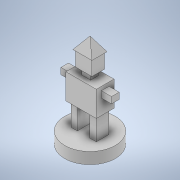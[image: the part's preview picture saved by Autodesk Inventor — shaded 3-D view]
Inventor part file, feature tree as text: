
AUTODESK INVENTOR PART (.ipt)
format: ipt  version: 2020 (Build 240168000, 168)  size: 219,648 bytes
history: native  units: in
note: dims shown in document units (in); Inventor stores cm internally (conversion verified against a paired STEP export)
features: extrude x10, sketch x10
ambient origin geometry x8: Origin, YZ Plane, XZ Plane, XY Plane, X Axis, Y Axis, Z Axis, Center Point
bodies: Solid1 (feature_tree)
feature tree (20):
  extrude  "Extrusion1"  Depth=0.45in TaperAngle=0.0deg
  extrude  "Extrusion2"  Depth=0.25in
  extrude  "Extrusion3"  Depth=0.25in
  extrude  "Extrusion4"  Depth=0.25in
  extrude  "Extrusion5"  Depth=0.5in
  extrude  "Extrusion6"  Depth=0.1in
  extrude  "Extrusion7"  Depth=1.2in
  extrude  "Extrusion8"  Depth=1.0in TaperAngle=0.0deg
  sketch  "Sketch9"  dims[d19=0.2in d20=0.6in]
  sketch  "Sketch10"  dims[d21=0.3in d22=0.25in d23=0.3in d24=0.4in d25=0.0in d26=0.2in d27=0.6in d28=0.25in d29=0.3in d30=0.4in d31=0.0in d32=0.425in d33=0.425in d34=0.2in d35=0.3in d36=0.25in d37=0.0in d38=0.15in d39=0.65in d40=0.6in d41=0.0in d42=0.05in d43=0.05in d44=0.6in d45=0.5in d46=0.0in d47=0.3in d48=0.6in d49=0.0in d50=0.8in d51=0.0in d52=0.5in d53=0.0344in]
  extrude  "Extrusion9"  Depth=0.6in
  extrude  "Extrusion10"  Depth=0.25in
  sketch  "Sketch1"  dims[d0=2.0in d1=0.45in d2=0.0in]
  sketch  "Sketch2"  dims[d3=0.25in d4=0.25in]
  sketch  "Sketch3"  dims[d5=0.25in d6=0.25in]
  sketch  "Sketch4"  dims[d7=0.5in d8=0.25in]
  sketch  "Sketch5"  dims[d9=0.25in d10=0.5in]
  sketch  "Sketch6"  dims[d11=0.9in d12=0.0in d13=0.1in]
  sketch  "Sketch7"  dims[d14=0.1in d15=1.2in]
  sketch  "Sketch8"  dims[d16=0.7in d17=1.0in d18=0.0in]
